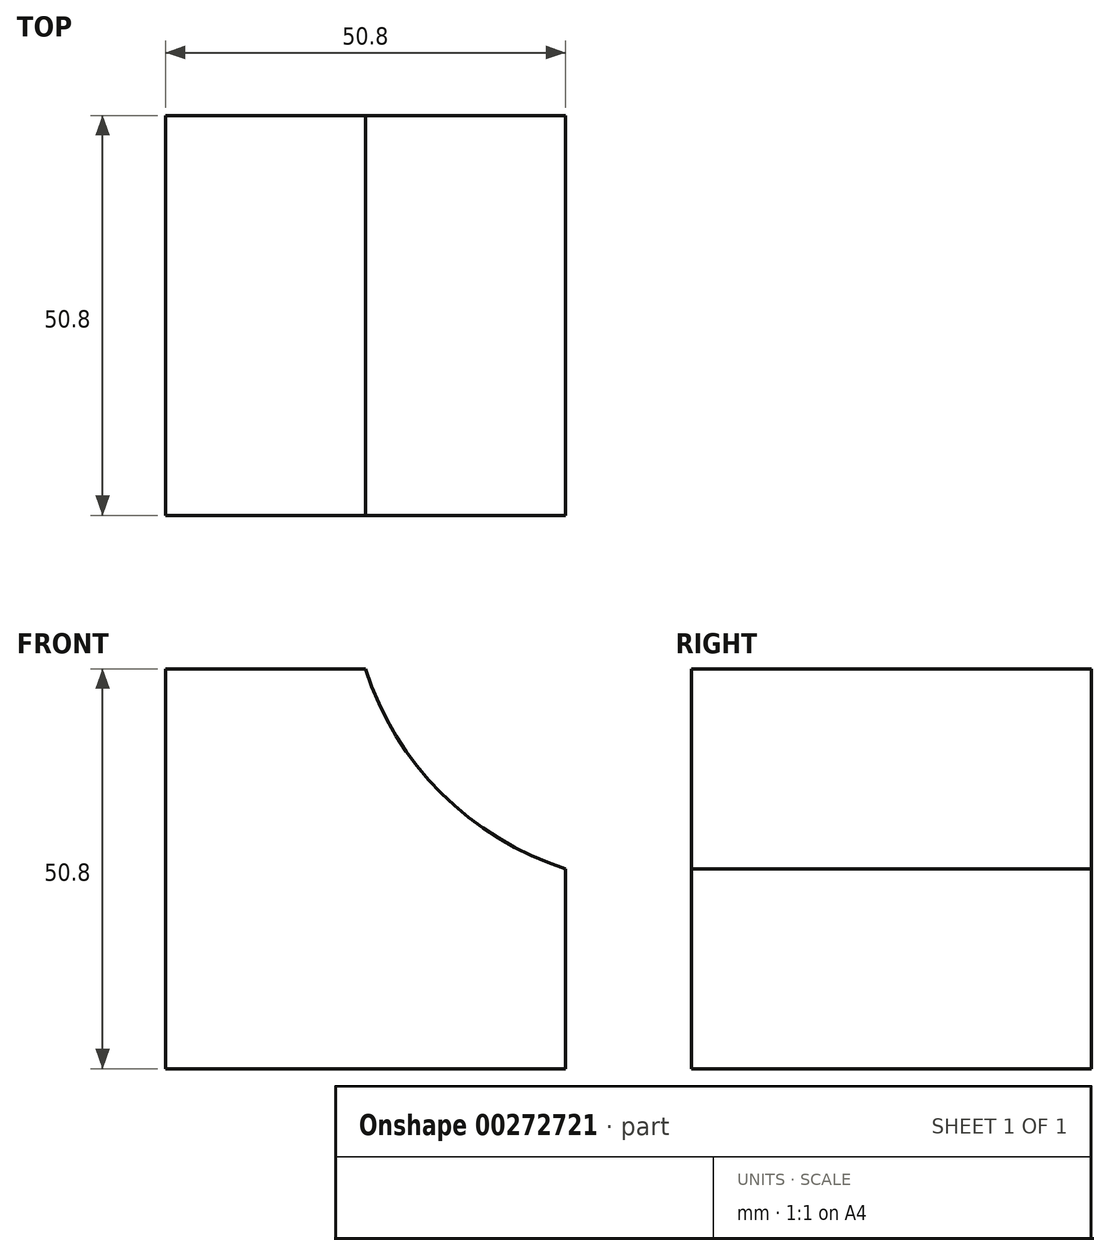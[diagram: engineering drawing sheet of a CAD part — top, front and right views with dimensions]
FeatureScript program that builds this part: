
annotation { "Feature Type Name" : "Feature", "Feature Type Description" : "" }
export const myFeature = defineFeature(function(context is Context, id is Id, definition is map)
    precondition{}
    {
        {
            var Q0;
            Q0=qCreatedBy(makeId("Front.planeOp"),FACE);
            var sketch = newSketch(context, id + "F0", { "sketchPlane" : qUnion([Q0])});
            skLineSegment(sketch, "E0", {"start": v(0, 0) * mm, "end": v(-50.8, 0) * mm});
            skLineSegment(sketch, "E1", {"start": v(-50.8, 0) * mm, "end": v(-50.8, 50.8) * mm});
            skLineSegment(sketch, "E2", {"start": v(-50.8, 50.8) * mm, "end": v(-25.4, 50.8) * mm});
            skLineSegment(sketch, "E3", {"start": v(0, 25.4) * mm, "end": v(0, 0) * mm});
            skArc(sketch, "E4", {"start": v(-25.4, 50.8) * mm, "mid": v(-15.8, 35) * mm, "end": v(0, 25.4) * mm});
            skSolve(sketch);
        }
        {
            var Q0;
            Q0 = qSketchRegion(id + "F0", true);
            extrude(context, id + "F1", {"entities" : qUnion([Q0]), "depth" : 50.8 * mm});
        }
    });
